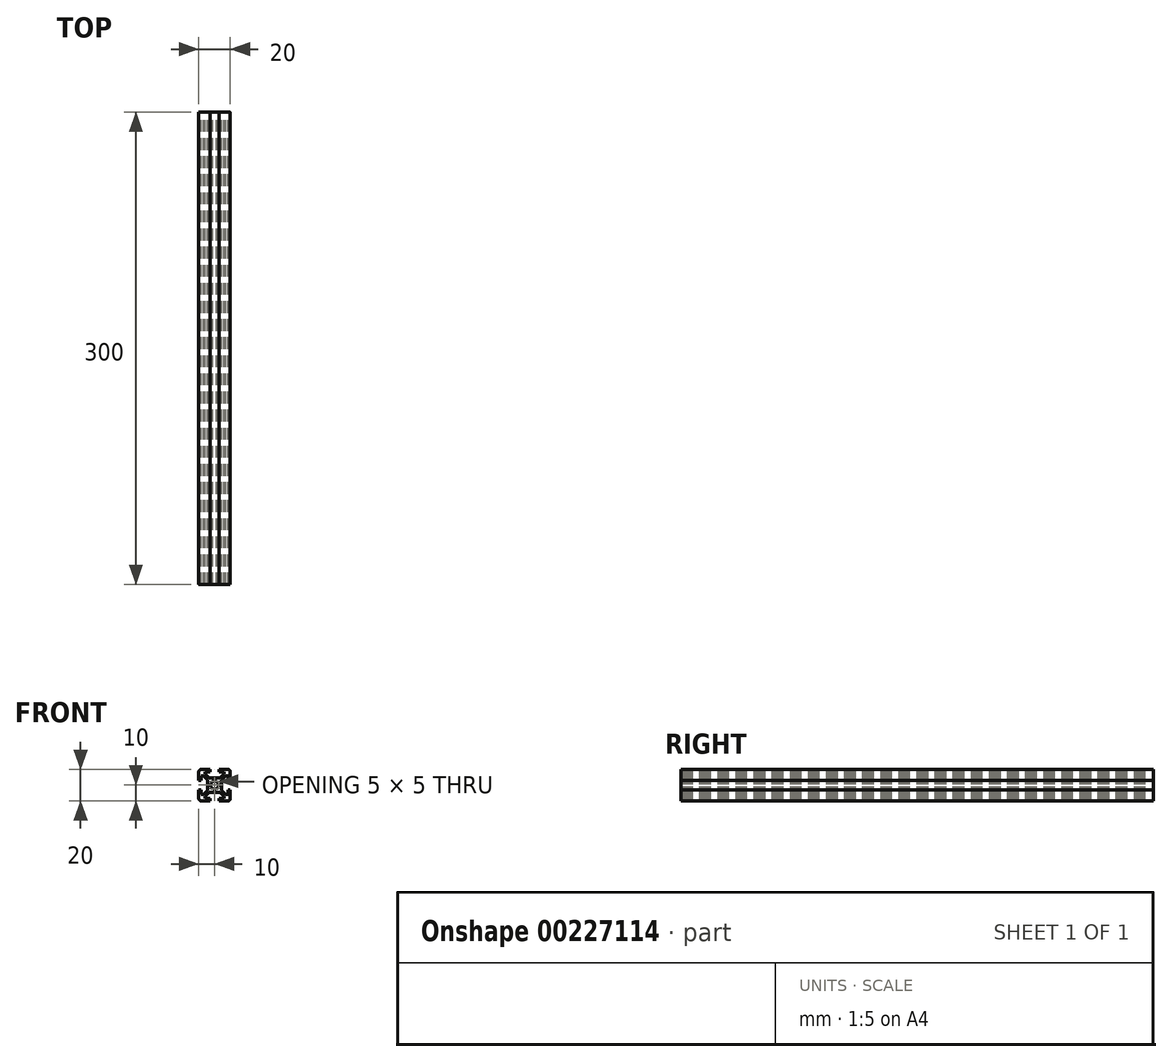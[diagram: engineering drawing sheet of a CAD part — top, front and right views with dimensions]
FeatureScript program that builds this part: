
annotation { "Feature Type Name" : "Feature", "Feature Type Description" : "" }
export const myFeature = defineFeature(function(context is Context, id is Id, definition is map)
    precondition{}
    {
        {
            var Q0;
            Q0=qCreatedBy(makeId("Front.planeOp"),FACE);
            var sketch = newSketch(context, id + "F0", { "sketchPlane" : qUnion([Q0])});
            skLineSegment(sketch, "E0.bottom", {"start": v(8.5, -10) * mm, "end": v(3, -10) * mm});
            skLineSegment(sketch, "E0.top", {"start": v(8.5, 10) * mm, "end": v(3, 10) * mm});
            skLineSegment(sketch, "E0.left", {"start": v(10, -8.5) * mm, "end": v(10, -3) * mm});
            skLineSegment(sketch, "E0.right", {"start": v(-10, -8.5) * mm, "end": v(-10, -3) * mm});
            skPoint(sketch, "E0.middle", {"position": v(0, 0) * mm});
            skLineSegment(sketch, "E1.bottom", {"start": v(6, -8.5) * mm, "end": v(3, -8.5) * mm});
            skLineSegment(sketch, "E1.top", {"start": v(6, 8.5) * mm, "end": v(3, 8.5) * mm});
            skLineSegment(sketch, "E1.left", {"start": v(8.5, -6) * mm, "end": v(8.5, -3) * mm});
            skLineSegment(sketch, "E1.right", {"start": v(-8.5, -6) * mm, "end": v(-8.5, -3) * mm});
            skLineSegment(sketch, "E2.bottom", {"start": v(3.44, -4.5) * mm, "end": v(-3.44, -4.5) * mm});
            skLineSegment(sketch, "E2.top", {"start": v(3.44, 4.5) * mm, "end": v(-3.44, 4.5) * mm});
            skLineSegment(sketch, "E2.left", {"start": v(4.5, -3.44) * mm, "end": v(4.5, 3.44) * mm});
            skLineSegment(sketch, "E2.right", {"start": v(-4.5, -3.44) * mm, "end": v(-4.5, 3.44) * mm});
            skLineSegment(sketch, "E3.bottom", {"start": v(8.5, -6) * mm, "end": v(7.06, -6) * mm});
            skLineSegment(sketch, "E3.top", {"start": v(8.5, 6) * mm, "end": v(7.06, 6) * mm});
            skLineSegment(sketch, "E4.left", {"start": v(6, -8.5) * mm, "end": v(6, -7.06) * mm});
            skLineSegment(sketch, "E4.right", {"start": v(-6, -8.5) * mm, "end": v(-6, -7.06) * mm});
            skPoint(sketch, "E5.orphan", {"position": v(-8.5, 8.5) * mm});
            skPoint(sketch, "E6.orphan", {"position": v(8.5, 8.5) * mm});
            skPoint(sketch, "E7.orphan", {"position": v(8.5, -8.5) * mm});
            skPoint(sketch, "E8.orphan", {"position": v(-8.5, -8.5) * mm});
            skLineSegment(sketch, "E9.trimOffspring", {"start": v(-6, 7.06) * mm, "end": v(-6, 8.5) * mm});
            skLineSegment(sketch, "E10.trimOffspring", {"start": v(-7.06, 6) * mm, "end": v(-8.5, 6) * mm});
            skLineSegment(sketch, "E11.trimOffspring", {"start": v(6, 7.06) * mm, "end": v(6, 8.5) * mm});
            skLineSegment(sketch, "E12.trimOffspring", {"start": v(-7.06, -6) * mm, "end": v(-8.5, -6) * mm});
            skLineSegment(sketch, "E13", {"start": v(-10, 10) * mm, "end": v(0, 0) * mm, "construction": true});
            skLineSegment(sketch, "E14", {"start": v(10, 10) * mm, "end": v(0, 0) * mm, "construction": true});
            skLineSegment(sketch, "E15", {"start": v(-6, 7.06) * mm, "end": v(-3.44, 4.5) * mm});
            skPoint(sketch, "E15.endSnap0", {"position": v(7.25, -6) * mm});
            skLineSegment(sketch, "E16", {"start": v(6, -7.06) * mm, "end": v(3.44, -4.5) * mm});
            skLineSegment(sketch, "E17", {"start": v(7.06, 6) * mm, "end": v(4.5, 3.44) * mm});
            skLineSegment(sketch, "E18", {"start": v(6, 7.06) * mm, "end": v(3.44, 4.5) * mm});
            skPoint(sketch, "E19.orphan", {"position": v(6, -6) * mm});
            skPoint(sketch, "E20.orphan", {"position": v(-4.5, -4.5) * mm});
            skPoint(sketch, "E21.orphan", {"position": v(-4.5, 4.5) * mm});
            skPoint(sketch, "E22.orphan", {"position": v(4.5, 4.5) * mm});
            skPoint(sketch, "E23.orphan", {"position": v(4.5, -4.5) * mm});
            skLineSegment(sketch, "E24.trimOffspring", {"start": v(4.5, -3.44) * mm, "end": v(7.06, -6) * mm});
            skLineSegment(sketch, "E25.trimOffspring", {"start": v(-3.44, -4.5) * mm, "end": v(-6, -7.06) * mm});
            skLineSegment(sketch, "E26.trimOffspring", {"start": v(-4.5, -3.44) * mm, "end": v(-7.06, -6) * mm});
            skLineSegment(sketch, "E27.trimOffspring", {"start": v(-4.5, 3.44) * mm, "end": v(-7.06, 6) * mm});
            skLineSegment(sketch, "E28.bottom", {"start": v(8.5, -3) * mm, "end": v(10, -3) * mm});
            skLineSegment(sketch, "E28.top", {"start": v(8.5, 3) * mm, "end": v(10, 3) * mm});
            skPoint(sketch, "E28.middle", {"position": v(10, 0) * mm});
            skLineSegment(sketch, "E29.left", {"start": v(3, 8.5) * mm, "end": v(3, 10) * mm});
            skLineSegment(sketch, "E29.right", {"start": v(-3, 8.5) * mm, "end": v(-3, 10) * mm});
            skPoint(sketch, "E29.middle", {"position": v(0, 10) * mm});
            skLineSegment(sketch, "E30.bottom", {"start": v(-8.5, 3) * mm, "end": v(-10, 3) * mm});
            skLineSegment(sketch, "E30.top", {"start": v(-8.5, -3) * mm, "end": v(-10, -3) * mm});
            skPoint(sketch, "E30.middle", {"position": v(-10, 0) * mm});
            skLineSegment(sketch, "E31.left", {"start": v(3, -8.5) * mm, "end": v(3, -10) * mm});
            skLineSegment(sketch, "E31.right", {"start": v(-3, -8.5) * mm, "end": v(-3, -10) * mm});
            skPoint(sketch, "E31.middle", {"position": v(0, -10) * mm});
            skPoint(sketch, "E32.orphan", {"position": v(3, 11.5) * mm});
            skPoint(sketch, "E33.orphan", {"position": v(-3, 11.5) * mm});
            skLineSegment(sketch, "E34.trimOffspring", {"start": v(-3, 10) * mm, "end": v(-8.5, 10) * mm});
            skLineSegment(sketch, "E35.trimOffspring", {"start": v(-3, 8.5) * mm, "end": v(-6, 8.5) * mm});
            skPoint(sketch, "E28.right.end.orphan", {"position": v(11.5, 3) * mm});
            skPoint(sketch, "E36.orphan", {"position": v(11.5, -3) * mm});
            skLineSegment(sketch, "E37.trimOffspring", {"start": v(10, 3) * mm, "end": v(10, 8.5) * mm});
            skLineSegment(sketch, "E38.trimOffspring", {"start": v(8.5, 3) * mm, "end": v(8.5, 6) * mm});
            skPoint(sketch, "E39.orphan", {"position": v(3, -11.5) * mm});
            skPoint(sketch, "E40.orphan", {"position": v(-3, -11.5) * mm});
            skLineSegment(sketch, "E41.trimOffspring", {"start": v(-3, -10) * mm, "end": v(-8.5, -10) * mm});
            skLineSegment(sketch, "E42.trimOffspring", {"start": v(-3, -8.5) * mm, "end": v(-6, -8.5) * mm});
            skPoint(sketch, "E30.right.end.orphan", {"position": v(-11.5, -3) * mm});
            skPoint(sketch, "E43.orphan", {"position": v(-11.5, 3) * mm});
            skLineSegment(sketch, "E44.trimOffspring", {"start": v(-10, 3) * mm, "end": v(-10, 8.5) * mm});
            skLineSegment(sketch, "E45.trimOffspring", {"start": v(-8.5, 3) * mm, "end": v(-8.5, 6) * mm});
            skLineSegment(sketch, "E46.trimOffspring", {"start": v(0, 0) * mm, "end": v(10, -10) * mm, "construction": true});
            skLineSegment(sketch, "E47.trimOffspring", {"start": v(0, 0) * mm, "end": v(-10, -10) * mm, "construction": true});
            skArc(sketch, "E48", {"start": v(1.16, 2.22) * mm, "mid": v(0, 2.5) * mm, "end": v(-1.16, 2.22) * mm});
            skLineSegment(sketch, "E49", {"start": v(-2.5, -1.44) * mm, "end": v(1.44, 2.5) * mm});
            skLineSegment(sketch, "E50", {"start": v(2.5, 1.44) * mm, "end": v(-1.44, -2.5) * mm});
            skLineSegment(sketch, "E51", {"start": v(1.44, -2.5) * mm, "end": v(-2.5, 1.44) * mm});
            skLineSegment(sketch, "E52", {"start": v(-1.44, 2.5) * mm, "end": v(2.5, -1.44) * mm});
            skLineSegment(sketch, "E53", {"start": v(2.5, 1.44) * mm, "end": v(2.5, -1.44) * mm, "construction": true});
            skLineSegment(sketch, "E54", {"start": v(1.44, -2.5) * mm, "end": v(-1.44, -2.5) * mm, "construction": true});
            skLineSegment(sketch, "E55", {"start": v(-2.5, -1.44) * mm, "end": v(-2.5, 1.44) * mm, "construction": true});
            skLineSegment(sketch, "E56", {"start": v(-1.44, 2.5) * mm, "end": v(1.44, 2.5) * mm, "construction": true});
            skLineSegment(sketch, "E57", {"start": v(-1.44, 2.5) * mm, "end": v(-2.5, 1.44) * mm});
            skLineSegment(sketch, "E58", {"start": v(1.44, 2.5) * mm, "end": v(2.5, 1.44) * mm});
            skLineSegment(sketch, "E59", {"start": v(2.5, -1.44) * mm, "end": v(1.44, -2.5) * mm});
            skLineSegment(sketch, "E60", {"start": v(-1.44, -2.5) * mm, "end": v(-2.5, -1.44) * mm});
            skArc(sketch, "E61.trimOffspring", {"start": v(-2.22, 1.16) * mm, "mid": v(-2.5, 0) * mm, "end": v(-2.22, -1.16) * mm});
            skArc(sketch, "E62.trimOffspring", {"start": v(-1.16, -2.22) * mm, "mid": v(0, -2.5) * mm, "end": v(1.16, -2.22) * mm});
            skArc(sketch, "E63.trimOffspring", {"start": v(2.22, -1.16) * mm, "mid": v(2.5, 0) * mm, "end": v(2.22, 1.16) * mm});
            skPoint(sketch, "E64.visualSharp", {"position": v(10, 10) * mm});
            skArc(sketch, "E64.filletArc", {"start": v(10, 8.5) * mm, "mid": v(9.56, 9.56) * mm, "end": v(8.5, 10) * mm});
            skPoint(sketch, "E65.visualSharp", {"position": v(10, -10) * mm});
            skArc(sketch, "E65.filletArc", {"start": v(8.5, -10) * mm, "mid": v(9.56, -9.56) * mm, "end": v(10, -8.5) * mm});
            skPoint(sketch, "E66.visualSharp", {"position": v(-10, -10) * mm});
            skArc(sketch, "E66.filletArc", {"start": v(-10, -8.5) * mm, "mid": v(-9.56, -9.56) * mm, "end": v(-8.5, -10) * mm});
            skPoint(sketch, "E67.visualSharp", {"position": v(-10, 10) * mm});
            skArc(sketch, "E67.filletArc", {"start": v(-8.5, 10) * mm, "mid": v(-9.56, 9.56) * mm, "end": v(-10, 8.5) * mm});
            skSolve(sketch);
        }
        {
            assignVariable(context, id + "F2", {"name" : "Length", "anyValue" : 300});
        }
        {
            var Q0;
            Q0=qSketchRegion(id+"F0",true);
            extrude(context, id + "F1", {"entities" : qUnion([Q0]), "depth" : (getVariable(context, 'Length')) * mm});
        }
    });
